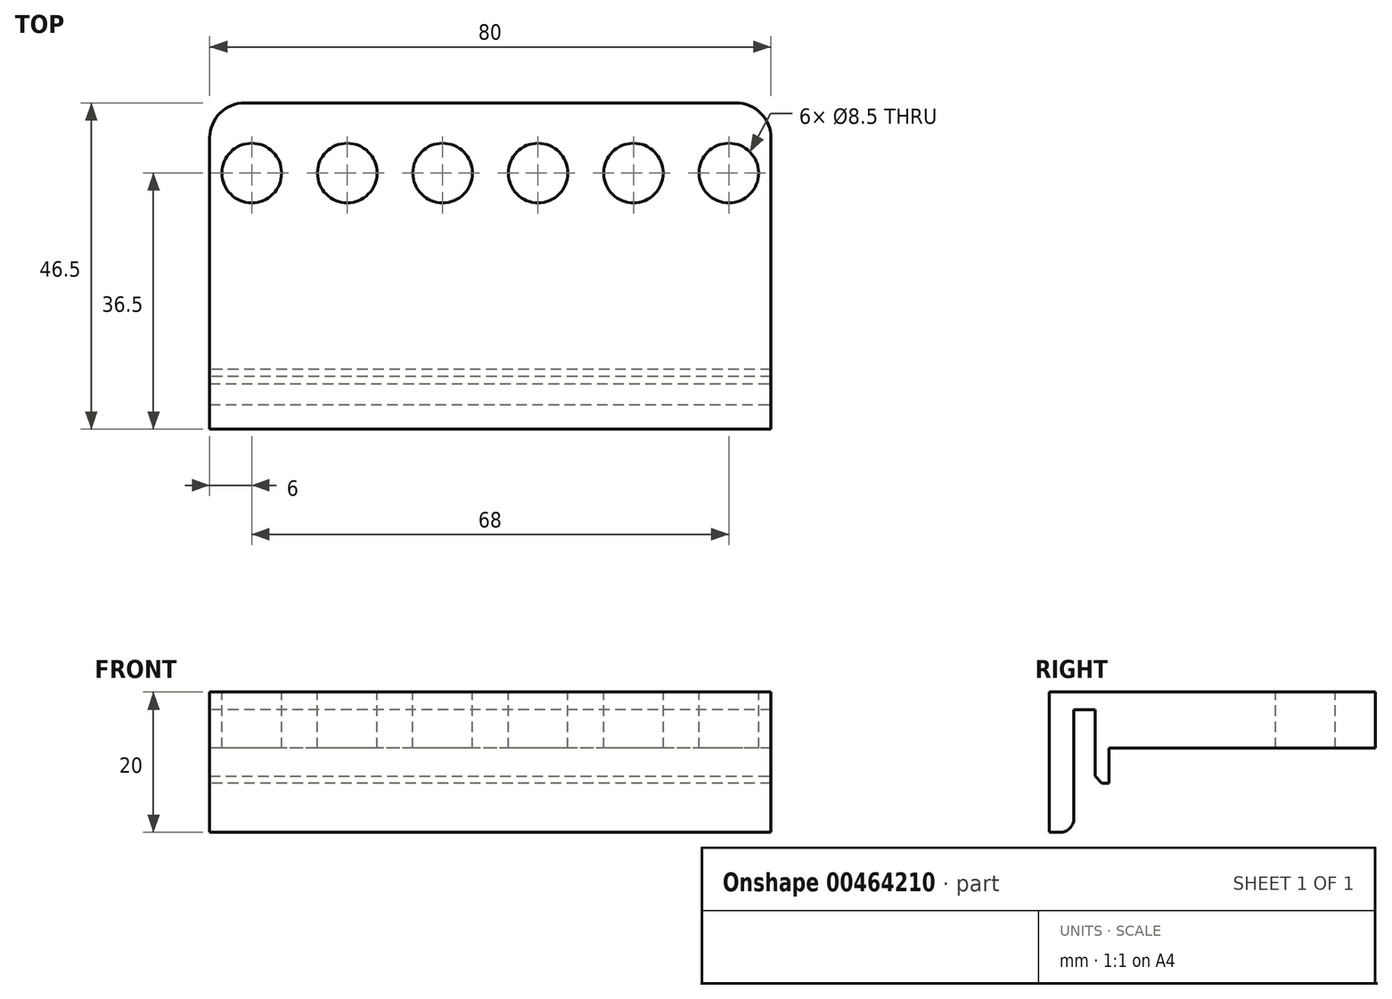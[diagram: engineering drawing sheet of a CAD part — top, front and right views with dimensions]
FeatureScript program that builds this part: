
annotation { "Feature Type Name" : "Feature", "Feature Type Description" : "" }
export const myFeature = defineFeature(function(context is Context, id is Id, definition is map)
    precondition{}
    {
        {
            var Q0;
            Q0=qCreatedBy(makeId("Top.planeOp"),FACE);
            var sketch = newSketch(context, id + "F0", { "sketchPlane" : qUnion([Q0])});
            skLineSegment(sketch, "E0.bottom", {"start": v(40, 20) * mm, "end": v(-40, 20) * mm});
            skLineSegment(sketch, "E0.top", {"start": v(40, -20) * mm, "end": v(-40, -20) * mm});
            skLineSegment(sketch, "E0.left", {"start": v(40, 20) * mm, "end": v(40, -20) * mm});
            skLineSegment(sketch, "E0.right", {"start": v(-40, 20) * mm, "end": v(-40, -20) * mm});
            skPoint(sketch, "E0.middle", {"position": v(0, 0) * mm});
            skLineSegment(sketch, "E1", {"start": v(-40, -20) * mm, "end": v(-40, -23) * mm});
            skLineSegment(sketch, "E2", {"start": v(-40, -23) * mm, "end": v(40, -23) * mm});
            skLineSegment(sketch, "E3", {"start": v(40, -23) * mm, "end": v(40, -20) * mm});
            skLineSegment(sketch, "E4.top", {"start": v(-40, -26.5) * mm, "end": v(40, -26.5) * mm});
            skLineSegment(sketch, "E4.left", {"start": v(-40, -23) * mm, "end": v(-40, -26.5) * mm});
            skLineSegment(sketch, "E4.right", {"start": v(40, -23) * mm, "end": v(40, -26.5) * mm});
            skSolve(sketch);
        }
        {
            var Q0;
            Q0=makeQuery(id+"F0.imprint","IMPRINT",FACE,{"disambiguationData":[TD([[makeQuery(id+"F0.imprint","IMPRINT",EDGE,{"derivedFrom":sQuery(id+"F0.wireOp",EDGE,"E0.bottom")}),1.0]])]});
            extrude(context, id + "F1", {"entities" : qUnion([Q0]), "oppositeDirection" : true, "depth" : 8 * mm});
        }
        {
            var Q0;
            Q0=makeQuery(id+"F0.imprint","IMPRINT",FACE,{"disambiguationData":[TD([[makeQuery(id+"F0.imprint","IMPRINT",EDGE,{"derivedFrom":sQuery(id+"F0.wireOp",EDGE,"E0.top")}),1.0]])]});
            extrude(context, id + "F2", {"entities" : qUnion([Q0]), "operationType" : NewBodyOperationType.ADD, "oppositeDirection" : true, "depth" : 2.5 * mm});
        }
        {
            var Q0;
            Q0=makeQuery(id+"F0.imprint","IMPRINT",FACE,{"disambiguationData":[TD([[makeQuery(id+"F0.imprint","IMPRINT",EDGE,{"derivedFrom":sQuery(id+"F0.wireOp",EDGE,"E2")}),-1.0]])]});
            extrude(context, id + "F3", {"entities" : qUnion([Q0]), "operationType" : NewBodyOperationType.ADD, "oppositeDirection" : true, "depth" : 20 * mm});
        }
        {
            var Q0;
            {var subQ0=sQuery(id+"F0.wireOp",EDGE,"E2");var subQ1=sQuery(id+"F0.wireOp",EDGE,"E0.top");Q0=makeQuery(id+"F3.boolean.opBoolean","MERGE",FACE,{"derivedFrom":[makeQuery(id+"F2.boolean.opBoolean","MERGE",FACE,{"derivedFrom":[makeQuery(id+"F1.opExtrude","CAP_FACE",FACE,{"disambiguationData":[OSD([sQuery(id+"F0.wireOp",EDGE,"E0.bottom"),subQ1,sQuery(id+"F0.wireOp",EDGE,"E0.left"),sQuery(id+"F0.wireOp",EDGE,"E0.right")])],"isStart":true}),makeQuery(id+"F2.opExtrude","CAP_FACE",FACE,{"disambiguationData":[OSD([subQ1,sQuery(id+"F0.wireOp",EDGE,"E1"),sQuery(id+"F0.wireOp",EDGE,"E3"),subQ0])],"isStart":true})]}),makeQuery(id+"F3.opExtrude","CAP_FACE",FACE,{"disambiguationData":[OSD([subQ0,sQuery(id+"F0.wireOp",EDGE,"E4.top"),sQuery(id+"F0.wireOp",EDGE,"E4.left"),sQuery(id+"F0.wireOp",EDGE,"E4.right")])],"isStart":true})]});}
            var sketch = newSketch(context, id + "F4", { "sketchPlane" : qUnion([Q0])});
            skLineSegment(sketch, "E5.0.0", {"start": v(40, -20) * mm, "end": v(-40, -20) * mm});
            skLineSegment(sketch, "E5.0.1", {"start": v(-40, -20) * mm, "end": v(-40, 20) * mm});
            skLineSegment(sketch, "E5.0.2", {"start": v(-40, 20) * mm, "end": v(40, 20) * mm});
            skLineSegment(sketch, "E5.0.3", {"start": v(40, 20) * mm, "end": v(40, -20) * mm});
            skLineSegment(sketch, "E6", {"start": v(40, 10) * mm, "end": v(34, 10) * mm, "construction": true});
            skLineSegment(sketch, "E7", {"start": v(34, 10) * mm, "end": v(20.4, 10) * mm, "construction": true});
            skLineSegment(sketch, "E8", {"start": v(20.4, 10) * mm, "end": v(6.8, 10) * mm, "construction": true});
            skLineSegment(sketch, "E9", {"start": v(6.8, 10) * mm, "end": v(-6.8, 10) * mm, "construction": true});
            skLineSegment(sketch, "E10", {"start": v(-6.8, 10) * mm, "end": v(-20.4, 10) * mm, "construction": true});
            skLineSegment(sketch, "E11", {"start": v(-20.4, 10) * mm, "end": v(-34, 10) * mm, "construction": true});
            skLineSegment(sketch, "E12", {"start": v(-34, 10) * mm, "end": v(-40, 10) * mm, "construction": true});
            skSolve(sketch);
        }
        {
            var Q0;
            Q0=sQuery(id+"F4.wireOp",VERTEX,"E11.end");
            var Q1;
            Q1=sQuery(id+"F4.wireOp",VERTEX,"E7.start");
            var Q2;
            Q2=sQuery(id+"F4.wireOp",VERTEX,"E9.start");
            var Q3;
            Q3=sQuery(id+"F4.wireOp",VERTEX,"E8.start");
            var Q4;
            Q4=sQuery(id+"F4.wireOp",VERTEX,"E10.end");
            var Q5;
            Q5=sQuery(id+"F4.wireOp",VERTEX,"E9.end");
            var Q6;
            Q6=makeQuery(id+"F1.opExtrude","SWEPT_BODY",BODY,{"disambiguationData":[OSD([sQuery(id+"F0.wireOp",EDGE,"E0.bottom"),sQuery(id+"F0.wireOp",EDGE,"E0.top"),sQuery(id+"F0.wireOp",EDGE,"E0.left"),sQuery(id+"F0.wireOp",EDGE,"E0.right")])]});
            hole(context, id + "F5", {"style" : HoleStyle.SIMPLE, "endStyle" : HoleEndStyle.THROUGH, "holeDiameter" : 8.5 * mm, "tappedDepth" : 7.05 * mm, "tapClearance" : 3, "locations" : qUnion([Q0, Q1, Q2, Q3, Q4, Q5]), "scope" : qUnion([Q6])});
        }
        {
            var Q0;
            Q0=makeQuery(id+"F3.opExtrude","CAP_EDGE",EDGE,{"disambiguationData":[OSD([sQuery(id+"F0.wireOp",EDGE,"E2")])],"isStart":false});
            fillet(context, id + "F6", {"entities" : qUnion([Q0]), "radius" : 2 * mm, "tangentPropagation" : true, "allowEdgeOverflow" : false});
        }
        {
            var Q0;
            Q0=makeQuery(id+"F1.opExtrude","SWEPT_EDGE",EDGE,{"disambiguationData":[OSD([sQuery(id+"F0.wireOp",EDGE,"E0.bottom"),sQuery(id+"F0.wireOp",EDGE,"E0.left")])]});
            var Q1;
            Q1=makeQuery(id+"F1.opExtrude","SWEPT_EDGE",EDGE,{"disambiguationData":[OSD([sQuery(id+"F0.wireOp",EDGE,"E0.bottom"),sQuery(id+"F0.wireOp",EDGE,"E0.right")])]});
            fillet(context, id + "F7", {"entities" : qUnion([Q0, Q1]), "radius" : 5 * mm, "tangentPropagation" : true, "allowEdgeOverflow" : false});
        }
        {
            var Q0;
            Q0=makeQuery(id+"F1.opExtrude","CAP_FACE",FACE,{"disambiguationData":[OSD([sQuery(id+"F0.wireOp",EDGE,"E0.bottom"),sQuery(id+"F0.wireOp",EDGE,"E0.top"),sQuery(id+"F0.wireOp",EDGE,"E0.left"),sQuery(id+"F0.wireOp",EDGE,"E0.right")])],"isStart":false});
            var sketch = newSketch(context, id + "F8", { "sketchPlane" : qUnion([Q0])});
            skLineSegment(sketch, "E13.0.0", {"start": v(-35, -20) * mm, "end": v(35, -20) * mm});
            skArc(sketch, "E13.0.1", {"start": v(35, -20) * mm, "mid": v(38.54, -18.54) * mm, "end": v(40, -15) * mm});
            skLineSegment(sketch, "E13.0.2", {"start": v(40, -15) * mm, "end": v(40, 20) * mm});
            skLineSegment(sketch, "E13.0.3", {"start": v(40, 20) * mm, "end": v(-40, 20) * mm});
            skLineSegment(sketch, "E13.0.4", {"start": v(-40, 20) * mm, "end": v(-40, -15) * mm});
            skArc(sketch, "E13.0.5", {"start": v(-40, -15) * mm, "mid": v(-38.54, -18.54) * mm, "end": v(-35, -20) * mm});
            skLineSegment(sketch, "E14", {"start": v(40, 18) * mm, "end": v(-40, 18) * mm});
            skSolve(sketch);
        }
        {
            var Q0;
            {var subQ0=sQuery(id+"F8.wireOp",EDGE,"E13.0.3");Q0=makeQuery(id+"F8.imprint","IMPRINT",FACE,{"disambiguationData":[TD([[makeQuery(id+"F8.imprint","IMPRINT",EDGE,{"derivedFrom":subQ0}),1.0]])]});}
            extrude(context, id + "F9", {"entities" : qUnion([Q0]), "operationType" : NewBodyOperationType.ADD, "depth" : 5 * mm});
        }
        {
            var Q0;
            Q0=makeQuery(id+"F9.opExtrude","CAP_EDGE",EDGE,{"disambiguationData":[OSD([sQuery(id+"F8.wireOp",EDGE,"E13.0.3")])],"isStart":false});
            chamfer(context, id + "F10", {"entities" : qUnion([Q0]), "width" : 1 * mm, "tangentPropagation" : true});
        }
    });
